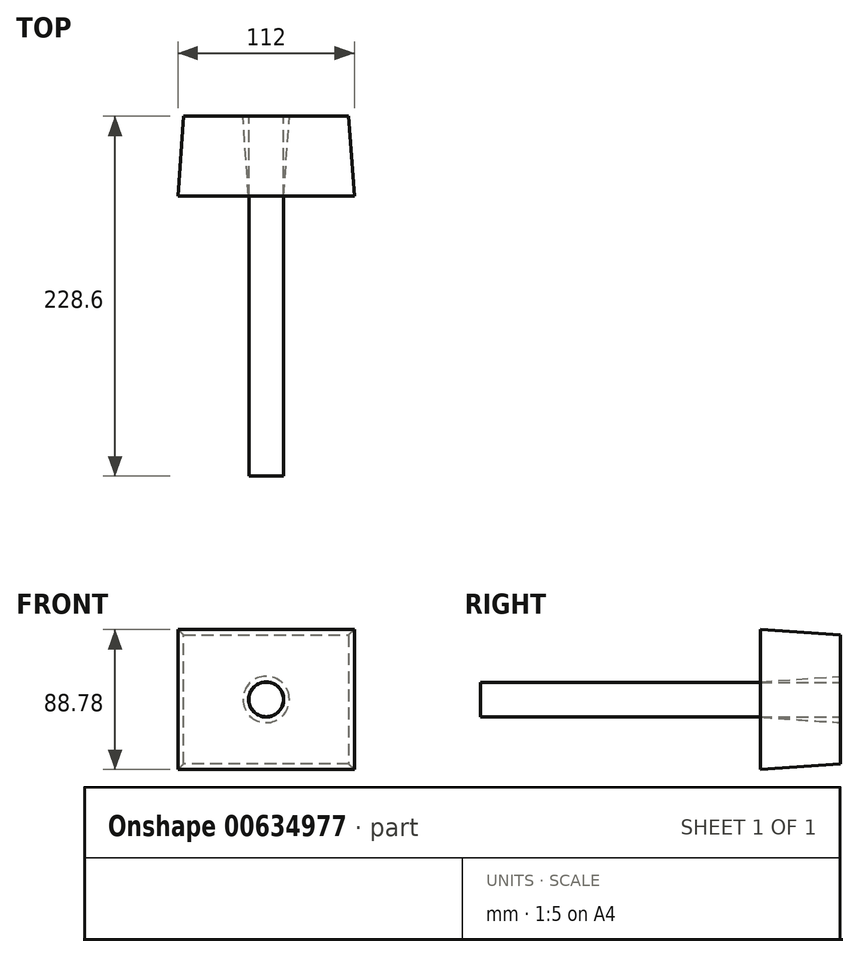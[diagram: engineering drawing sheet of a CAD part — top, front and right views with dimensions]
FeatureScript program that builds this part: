
annotation { "Feature Type Name" : "Feature", "Feature Type Description" : "" }
export const myFeature = defineFeature(function(context is Context, id is Id, definition is map)
    precondition{}
    {
        {
            var Q0;
            Q0=qCreatedBy(makeId("Front.planeOp"),FACE);
            var sketch = newSketch(context, id + "F0", { "sketchPlane" : qUnion([Q0])});
            skLineSegment(sketch, "E0.bottom", {"start": v(-52.45, 40.83) * mm, "end": v(52.45, 40.83) * mm});
            skLineSegment(sketch, "E0.top", {"start": v(-52.45, -40.83) * mm, "end": v(52.45, -40.83) * mm});
            skLineSegment(sketch, "E0.left", {"start": v(-52.45, 40.83) * mm, "end": v(-52.45, -40.83) * mm});
            skLineSegment(sketch, "E0.right", {"start": v(52.45, 40.83) * mm, "end": v(52.45, -40.83) * mm});
            skPoint(sketch, "E0.middle", {"position": v(0, 0) * mm});
            skCircle(sketch, "E1", {"center": v(0, 0) * mm, "radius": 14.72 * mm});
            skSolve(sketch);
        }
        {
            var Q0;
            Q0=makeQuery(id+"F0.imprint","IMPRINT",FACE,{"disambiguationData":[TD([[makeQuery(id+"F0.imprint","IMPRINT",EDGE,{"derivedFrom":sQuery(id+"F0.wireOp",EDGE,"E0.bottom")}),-1.0]])]});
            extrude(context, id + "F1", {"entities" : qUnion([Q0]), "depth" : 50.8 * mm, "offsetDistance" : 25.4 * mm, "hasDraft" : true, "draftAngle" : 4 * degree});
        }
        {
            var Q0;
            Q0=makeQuery(id+"F1.opExtrude","CAP_FACE",FACE,{"disambiguationData":[OSD([sQuery(id+"F0.wireOp",EDGE,"E0.bottom"),sQuery(id+"F0.wireOp",EDGE,"E0.top"),sQuery(id+"F0.wireOp",EDGE,"E0.left"),sQuery(id+"F0.wireOp",EDGE,"E0.right"),sQuery(id+"F0.wireOp",EDGE,"E1")])],"isStart":true});
            var sketch = newSketch(context, id + "F2", { "sketchPlane" : qUnion([Q0])});
            skCircle(sketch, "E2", {"center": v(0, 0) * mm, "radius": 10.96 * mm});
            skSolve(sketch);
        }
        {
            var Q0;
            Q0=makeQuery(id+"F2.imprint","IMPRINT",FACE,{"disambiguationData":[TD([[makeQuery(id+"F2.imprint","IMPRINT",EDGE,{"derivedFrom":sQuery(id+"F2.wireOp",EDGE,"E2")}),1.0]])]});
            extrude(context, id + "F3", {"entities" : qUnion([Q0]), "oppositeDirection" : true, "depth" : 228.6 * mm, "offsetDistance" : 25.4 * mm});
        }
    });
